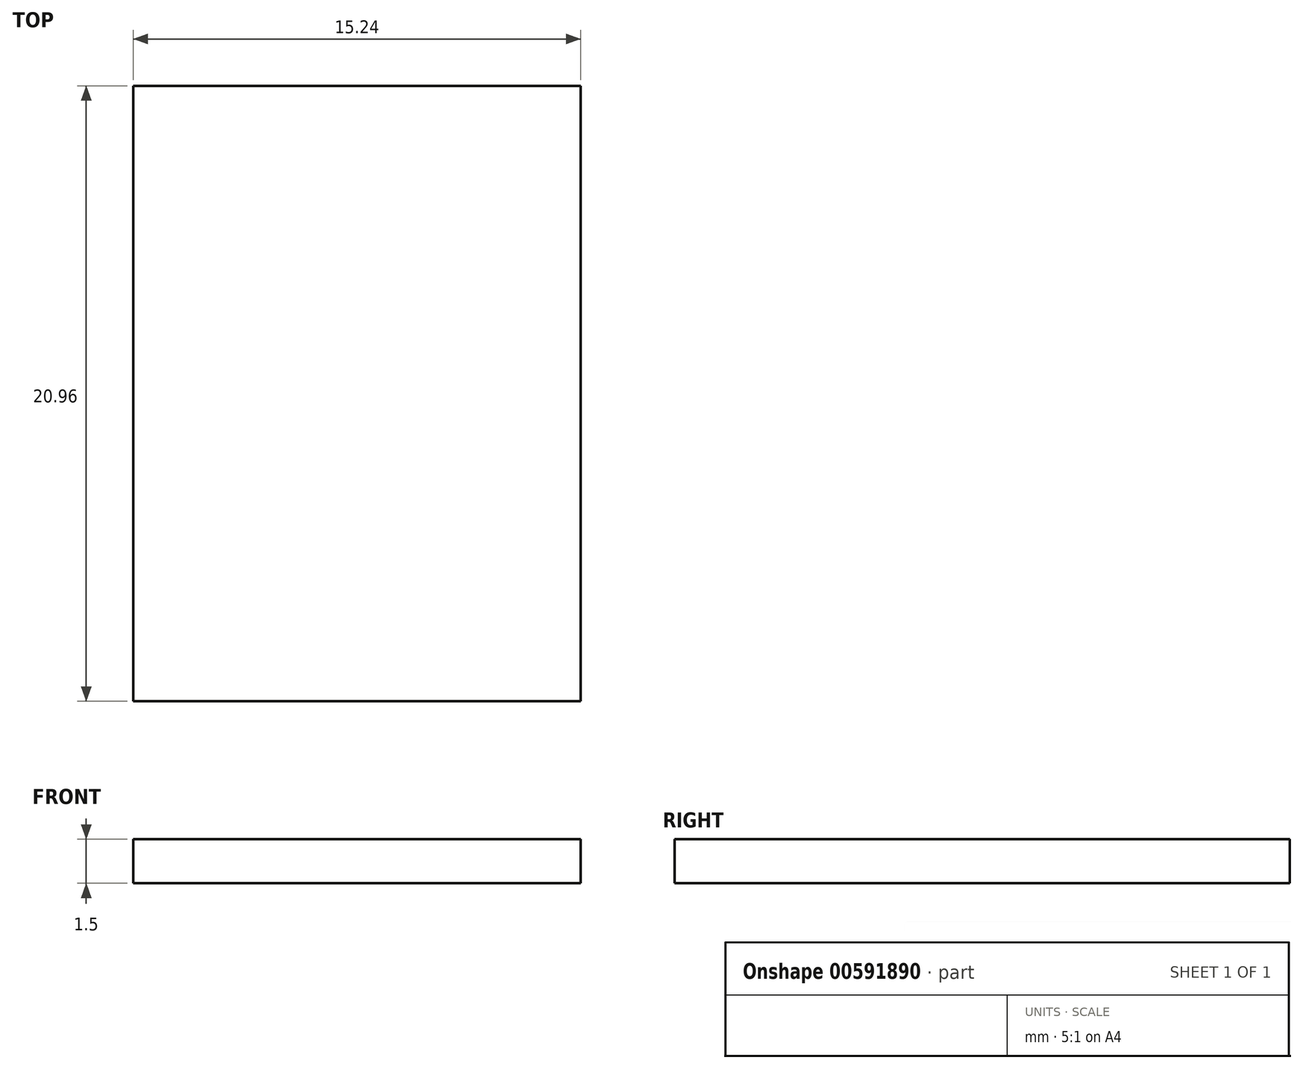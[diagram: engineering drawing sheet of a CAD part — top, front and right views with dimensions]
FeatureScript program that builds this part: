
annotation { "Feature Type Name" : "Feature", "Feature Type Description" : "" }
export const myFeature = defineFeature(function(context is Context, id is Id, definition is map)
    precondition{}
    {
        {
            var Q0;
            Q0=qCreatedBy(makeId("Top.planeOp"),FACE);
            var sketch = newSketch(context, id + "F0", { "sketchPlane" : qUnion([Q0])});
            skLineSegment(sketch, "E0.bottom", {"start": v(7.62, 10.48) * mm, "end": v(-7.62, 10.48) * mm});
            skLineSegment(sketch, "E0.top", {"start": v(7.62, -10.48) * mm, "end": v(-7.62, -10.48) * mm});
            skLineSegment(sketch, "E0.left", {"start": v(7.62, 10.48) * mm, "end": v(7.62, -10.48) * mm});
            skLineSegment(sketch, "E0.right", {"start": v(-7.62, 10.48) * mm, "end": v(-7.62, -10.48) * mm});
            skPoint(sketch, "E0.middle", {"position": v(0, 0) * mm});
            skSolve(sketch);
        }
        {
            var Q0;
            Q0=makeQuery(id+"F0.imprint","IMPRINT",FACE,{"disambiguationData":[TD([[makeQuery(id+"F0.imprint","IMPRINT",EDGE,{"derivedFrom":sQuery(id+"F0.wireOp",EDGE,"E0.bottom")}),1.0]])]});
            extrude(context, id + "F1", {"entities" : qUnion([Q0]), "depth" : 1.5 * mm, "offsetDistance" : 25 * mm});
        }
    });
